# Revit family: Bath-Freestanding-KOHLER-Volute-K-23746T_1
name_source: partatom
category: Plumbing Fixtures
units: mm (PartAtom-declared; Revit-internal decimal feet)

## family parameters
Cut with Voids When Loaded = No
Host = Face
OmniClass Number = 23.31.15.00
OmniClass Title = Bathtubs
Part Type = Normal
Room Calculation Point = No
Round Connector Dimension = Use Diameter
Shared = No

## types (2) — shared parameters
ADA Compliant = No
Assembly Code = D2010500
CW Connection = No
Cold Water Inlet = Cold Water Inlet
Date Modified = 05/12/2023
Default Elevation = 0"
Drain Included = No
Finish = KOHLER-Cast_Iron-7-Black_Black
Flow Rate = 0 GPM
HW Connection = No
Height = 23 7/16"
Hot Water Inlet = Hot Water Inlet
Length = 59 1/16"
Manufacturer = Kohler Co.
Master Format 2014 = 22 41 19
Master Format 2014 Name = Residential Bathtubs
Material = Cast Iron
Pressure = 0.00 psi
Product Documentation Link = https://files.kohler.com.cn
Product Name = Volute
Product Page URL = https://www.kohler.com.cn
URL = http://www.kohler.com.cn
Vent Connection = No
Waste Connection = Yes
Waste Water Outlet = Waste Water Outlet
WaterSense Certified = No
Width = 31 1/2"

## per-type parameters (varying)
| type | Description | Model | Type |
| 7-Black Black | 1.5m Freestanding Cast Iron Bathtub (Manchester United Limited Edition, Including Drainage) | K-23746T-7 | 1 |
| Grab Handle, 7-Black Black | 1.5m Freestanding Cast Iron Bathtub (Manchester United Limited Edition, Including Drainage, Including Handrails) | K-23746T-GR-7 | 2 |

## geometry (parser evidence)
native form markers: Sweep x4
no freeform markers — native parametric forms only
